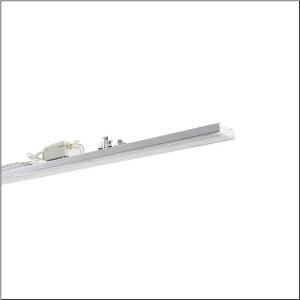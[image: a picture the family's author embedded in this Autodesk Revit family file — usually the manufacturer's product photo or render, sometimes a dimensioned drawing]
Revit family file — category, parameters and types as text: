
# Revit family: licross_r__21_recessed_ho_52te1edn4e5s_6cbf
name_source: partatom
category: Lighting Fixtures
units: mm (PartAtom-declared; Revit-internal decimal feet)

## family parameters
Cut with Voids When Loaded = No
Host = Face
Light Source = No
Part Type = Normal
Room Calculation Point = No
Round Connector Dimension = Use Diameter
Shared = No

## types (1)
- --- (1 x LED, 14620 lm, 84.6 W, 4000K)
    Apparent Load = 85 VA
    CIE Flux Codes = 85 95 99 100 100
    Color Rendering = 80
    Color Temperature = 4000K
    Default Elevation = 1800 mm
    Description = Licross® 21 Recessed HO, luminaire insert, of sheet steel, galvanised, coil coated, white, length: 1.500mm, width: 66mm, height: 67mm, LED rated luminous flux: 14.620lm, light colour: 840, control gear: DALI 2, with plug, 5-pole, with phase selection, mains connection: 220..240V, AC, 50/60Hz, rated input power: 85W, halogen-free wiring, primary light control with lens, of plastic, primary optical cover: cover, of PMMA, light emission: direct distribution, primary light characteristic: symmetric, protection rating (complete): IP54, insulation class (complete): insulation class I (protective earthing), certification: CE, ENEC, VDE, UKCA, protection symbol: D if used in an environment with non-conductive dust loads with corresponding accessories, impact resistance: IK06, permissible ambient temperature for indoor applications: -25..+30°C, corresponds to IFS (International Featured Standards) requirements for safety and quality in the food industry, reducing of maximum allowable ambient temperature of 5°C with ceiling mounting, LABS conformity tested according to VDMA 24364:2018-05, packaging unit: 1 piece
    Height = 58 mm
    Lamp = 1 x LED
    Lamp Light Flux = 14620 lm
    Lamp Power = 84.6 W
    Lamp count = 1
    Length = 1500 mm
    Luminous efficacy = 173 lm/W
    Manufacturer = Siteco
    ModVariant = No
    Model = 52TE1EDN4E5S
    Mounting Place = Ceiling
    Mounting Type = Pendant
    Number of Poles = 1
    OnlyDefault = Yes
    Power Factor = 1
    Product Name = Licross® 21 Recessed HO
    Product group = luminaire insert
    ProductGroupID = 901
    Protection Class = Protection class I
    Protection Degree = IP 54
    RLX_Detail_Level = 1
    RLX_Emergency_Light_Flux = 0 lm
    RLX_Emergency_Type = 0
    RLX_Emergency_Type_DB = No
    RlxData = <blob elided: 24789 chars, md5=9fe3e1d5>
    Socket = socket
    Standby Power = 0 W
    System Light Flux = 14620 lm
    System Power = 85 W
    Type Comments = factory setting: luminous flux: 100 % | dim-lin: 254 | 484 mA
    Type Image = l_1296930.jpg
    URL = http://relux.com
    VarID = @adj_056589
    Voltage = 0 V
    Weight = 0.00 kg
    Width = 66 mm

## geometry (parser evidence)
native form markers: Blend x4, Sweep x10
no freeform markers — native parametric forms only
